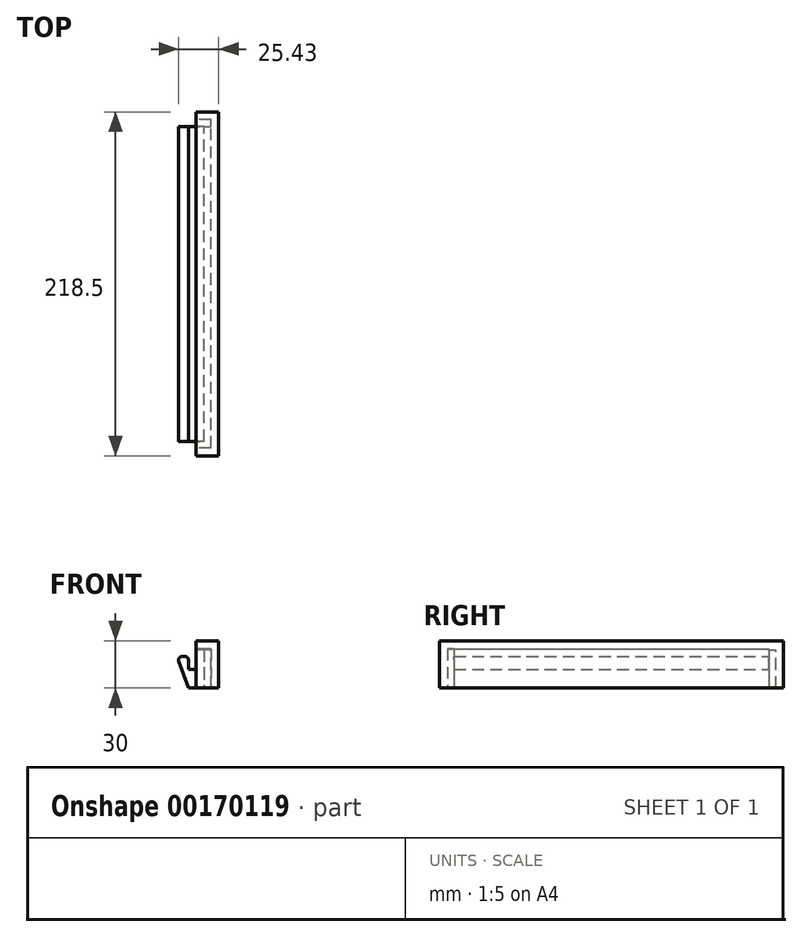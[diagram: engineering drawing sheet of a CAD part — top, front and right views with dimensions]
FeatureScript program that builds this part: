
annotation { "Feature Type Name" : "Feature", "Feature Type Description" : "" }
export const myFeature = defineFeature(function(context is Context, id is Id, definition is map)
    precondition{}
    {
        {
            var Q0;
            Q0=qCreatedBy(makeId("Front.planeOp"),FACE);
            var sketch = newSketch(context, id + "F0", { "sketchPlane" : qUnion([Q0])});
            skLineSegment(sketch, "E0.bottom", {"start": v(-6.57, 14.77) * mm, "end": v(0.43, 14.77) * mm});
            skLineSegment(sketch, "E0.right", {"start": v(0.43, 14.77) * mm, "end": v(0.43, -5.23) * mm});
            skLineSegment(sketch, "E1", {"start": v(-6.57, 14.77) * mm, "end": v(0.43, -5.23) * mm});
            skLineSegment(sketch, "E2.bottom", {"start": v(0.43, -5.23) * mm, "end": v(5.43, -5.23) * mm});
            skLineSegment(sketch, "E2.top", {"start": v(0.43, 6.77) * mm, "end": v(5.43, 6.77) * mm});
            skLineSegment(sketch, "E2.left", {"start": v(0.43, -5.23) * mm, "end": v(0.43, 6.77) * mm});
            skLineSegment(sketch, "E2.right", {"start": v(5.43, -5.23) * mm, "end": v(5.43, 6.77) * mm});
            skLineSegment(sketch, "E3.bottom", {"start": v(5.43, -5.23) * mm, "end": v(10.43, -5.23) * mm});
            skLineSegment(sketch, "E3.top", {"start": v(5.43, 24.77) * mm, "end": v(19.68, 24.77) * mm});
            skLineSegment(sketch, "E3.left", {"start": v(5.43, -5.23) * mm, "end": v(5.43, 24.77) * mm});
            skLineSegment(sketch, "E3.right", {"start": v(19.68, -5.23) * mm, "end": v(19.68, 24.77) * mm});
            skLineSegment(sketch, "E4.bottom", {"start": v(10.43, 19.77) * mm, "end": v(14.68, 19.77) * mm});
            skLineSegment(sketch, "E4.left", {"start": v(10.43, 19.77) * mm, "end": v(10.43, -5.23) * mm});
            skLineSegment(sketch, "E4.right", {"start": v(14.68, 19.77) * mm, "end": v(14.68, -5.23) * mm});
            skPoint(sketch, "E5", {"position": v(12.55, -5.23) * mm});
            skLineSegment(sketch, "E6", {"start": v(14.68, -5.23) * mm, "end": v(19.68, -5.23) * mm});
            skSolve(sketch);
        }
        {
            var Q0;
            Q0 = qSketchRegion(id + "F0", true);
            extrude(context, id + "F1", {"entities" : qUnion([Q0]), "depth" : 200 * mm});
        }
        {
            var Q0;
            Q0=makeQuery(id+"F1.opExtrude","SWEPT_EDGE",EDGE,{"disambiguationData":[OSD([sQuery(id+"F0.wireOp",EDGE,"E0.bottom"),sQuery(id+"F0.wireOp",EDGE,"E1")])]});
            var Q1;
            Q1=makeQuery(id+"F1.opExtrude","SWEPT_EDGE",EDGE,{"disambiguationData":[OSD([sQuery(id+"F0.wireOp",EDGE,"E0.bottom"),sQuery(id+"F0.wireOp",EDGE,"E0.right")])]});
            fillet(context, id + "F2", {"entities" : qUnion([Q0, Q1]), "radius" : 2 * mm, "tangentPropagation" : true, "allowEdgeOverflow" : false});
        }
        {
            var Q0;
            Q0=makeQuery(id+"F1.opExtrude","SWEPT_FACE",FACE,{"disambiguationData":[OSD([sQuery(id+"F0.wireOp",EDGE,"E3.top")])]});
            var sketch = newSketch(context, id + "F3", { "sketchPlane" : qUnion([Q0])});
            skLineSegment(sketch, "E7.bottom", {"start": v(19.68, 0) * mm, "end": v(5.43, 0) * mm});
            skLineSegment(sketch, "E7.top", {"start": v(19.68, 9.25) * mm, "end": v(5.43, 9.25) * mm});
            skLineSegment(sketch, "E7.left", {"start": v(19.68, 0) * mm, "end": v(19.68, 9.25) * mm});
            skLineSegment(sketch, "E7.right", {"start": v(5.43, 0) * mm, "end": v(5.43, 9.25) * mm});
            skSolve(sketch);
        }
        {
            var Q0;
            Q0 = qSketchRegion(id + "F3", true);
            extrude(context, id + "F4", {"entities" : qUnion([Q0]), "operationType" : NewBodyOperationType.ADD, "oppositeDirection" : true, "depth" : 30 * mm});
        }
        {
            var Q0;
            Q0=makeQuery(id+"F4.boolean.opBoolean","MERGE",FACE,{"derivedFrom":[makeQuery(id+"F1.opExtrude","SWEPT_FACE",FACE,{"disambiguationData":[OSD([sQuery(id+"F0.wireOp",EDGE,"E3.left")])]}),makeQuery(id+"F4.opExtrude","SWEPT_FACE",FACE,{"disambiguationData":[OSD([sQuery(id+"F3.wireOp",EDGE,"E7.right")])]})]});
            var sketch = newSketch(context, id + "F5", { "sketchPlane" : qUnion([Q0])});
            skPoint(sketch, "E8.oppositeSnap0", {"position": v(-4.25, -5.23) * mm});
            skLineSegment(sketch, "E8.bottom", {"start": v(0, -5.23) * mm, "end": v(-4.25, -5.23) * mm});
            skLineSegment(sketch, "E8.top", {"start": v(0, 19.05) * mm, "end": v(-4.25, 19.05) * mm});
            skLineSegment(sketch, "E8.left", {"start": v(0, -5.23) * mm, "end": v(0, 19.05) * mm});
            skLineSegment(sketch, "E8.right", {"start": v(-4.25, -5.23) * mm, "end": v(-4.25, 19.05) * mm});
            skSolve(sketch);
        }
        {
            var Q0;
            {var subQ2=sQuery(id+"F5.wireOp",EDGE,"E8.bottom");Q0=makeQuery(id+"F5.imprint","IMPRINT",FACE,{"disambiguationData":[TD([[makeQuery(id+"F5.imprint","IMPRINT",EDGE,{"derivedFrom":subQ2}),-1.0]])]});}
            extrude(context, id + "F6", {"entities" : qUnion([Q0]), "operationType" : NewBodyOperationType.REMOVE, "oppositeDirection" : true, "depth" : 9.25 * mm});
        }
        {
            var Q0;
            Q0=makeQuery(id+"F4.boolean.opBoolean","MERGE",FACE,{"derivedFrom":[makeQuery(id+"F1.opExtrude","SWEPT_FACE",FACE,{"disambiguationData":[OSD([sQuery(id+"F0.wireOp",EDGE,"E3.top")])]}),makeQuery(id+"F4.opExtrude","CAP_FACE",FACE,{"disambiguationData":[OSD([sQuery(id+"F3.wireOp",EDGE,"E7.bottom"),sQuery(id+"F3.wireOp",EDGE,"E7.top"),sQuery(id+"F3.wireOp",EDGE,"E7.left"),sQuery(id+"F3.wireOp",EDGE,"E7.right")])],"isStart":true})]});
            var sketch = newSketch(context, id + "F7", { "sketchPlane" : qUnion([Q0])});
            skLineSegment(sketch, "E9.bottom", {"start": v(5.43, -200) * mm, "end": v(19.68, -200) * mm});
            skLineSegment(sketch, "E9.top", {"start": v(5.43, -209.25) * mm, "end": v(19.68, -209.25) * mm});
            skLineSegment(sketch, "E9.left", {"start": v(5.43, -200) * mm, "end": v(5.43, -209.25) * mm});
            skLineSegment(sketch, "E9.right", {"start": v(19.68, -200) * mm, "end": v(19.68, -209.25) * mm});
            skSolve(sketch);
        }
        {
            var Q0;
            Q0 = qSketchRegion(id + "F7", true);
            extrude(context, id + "F8", {"entities" : qUnion([Q0]), "operationType" : NewBodyOperationType.ADD, "oppositeDirection" : true, "depth" : 30 * mm});
        }
        {
            var Q0;
            {var subQ2=sQuery(id+"F0.wireOp",EDGE,"E3.left");var subQ3=sQuery(id+"F3.wireOp",EDGE,"E7.right");var subQ4=sQuery(id+"F0.wireOp",EDGE,"E6");var subQ8=sQuery(id+"F0.wireOp",EDGE,"E3.bottom");var subQ10=sQuery(id+"F0.wireOp",EDGE,"E2.bottom");var subQ11=sQuery(id+"F0.wireOp",EDGE,"E1");var subQ15=sQuery(id+"F3.wireOp",EDGE,"E7.top");var subQ16=sQuery(id+"F3.wireOp",EDGE,"E7.left");var subQ19=makeQuery(id+"F4.boolean.opBoolean","MERGE",FACE,{"derivedFrom":[makeQuery(id+"F1.opExtrude","SWEPT_FACE",FACE,{"disambiguationData":[OSD([subQ10,subQ8])]}),makeQuery(id+"F1.opExtrude","SWEPT_FACE",FACE,{"disambiguationData":[OSD([subQ4])]}),makeQuery(id+"F4.opExtrude","CAP_FACE",FACE,{"disambiguationData":[OSD([sQuery(id+"F3.wireOp",EDGE,"E7.bottom"),subQ15,subQ16,subQ3])],"isStart":false})]});Q0=makeQuery(id+"F8.boolean.opBoolean","MERGE",FACE,{"derivedFrom":[makeQuery(id+"F6.boolean.opBoolean","SPLIT",FACE,{"disambiguationData":[TD([makeQuery(id+"F1.opExtrude","SWEPT_FACE",FACE,{"disambiguationData":[OSD([subQ11])]})])],"derivedFrom":subQ19}),makeQuery(id+"F6.boolean.opBoolean","SPLIT",FACE,{"disambiguationData":[TD([makeQuery(id+"F1.opExtrude","SWEPT_FACE",FACE,{"disambiguationData":[OSD([subQ2])]})])],"derivedFrom":subQ19}),makeQuery(id+"F8.opExtrude","CAP_FACE",FACE,{"disambiguationData":[OSD([sQuery(id+"F7.wireOp",EDGE,"E9.bottom"),sQuery(id+"F7.wireOp",EDGE,"E9.top"),sQuery(id+"F7.wireOp",EDGE,"E9.left"),sQuery(id+"F7.wireOp",EDGE,"E9.right")])],"isStart":false})]});}
            var sketch = newSketch(context, id + "F9", { "sketchPlane" : qUnion([Q0])});
            skLineSegment(sketch, "E10.bottom", {"start": v(14.68, 200) * mm, "end": v(5.43, 200) * mm});
            skLineSegment(sketch, "E10.top", {"start": v(14.68, 204.25) * mm, "end": v(5.43, 204.25) * mm});
            skLineSegment(sketch, "E10.left", {"start": v(14.68, 200) * mm, "end": v(14.68, 204.25) * mm});
            skLineSegment(sketch, "E10.right", {"start": v(5.43, 200) * mm, "end": v(5.43, 204.25) * mm});
            skSolve(sketch);
        }
        {
            var Q0;
            Q0 = qSketchRegion(id + "F9", true);
            extrude(context, id + "F10", {"entities" : qUnion([Q0]), "operationType" : NewBodyOperationType.REMOVE, "oppositeDirection" : true, "depth" : 25 * mm});
        }
    });
